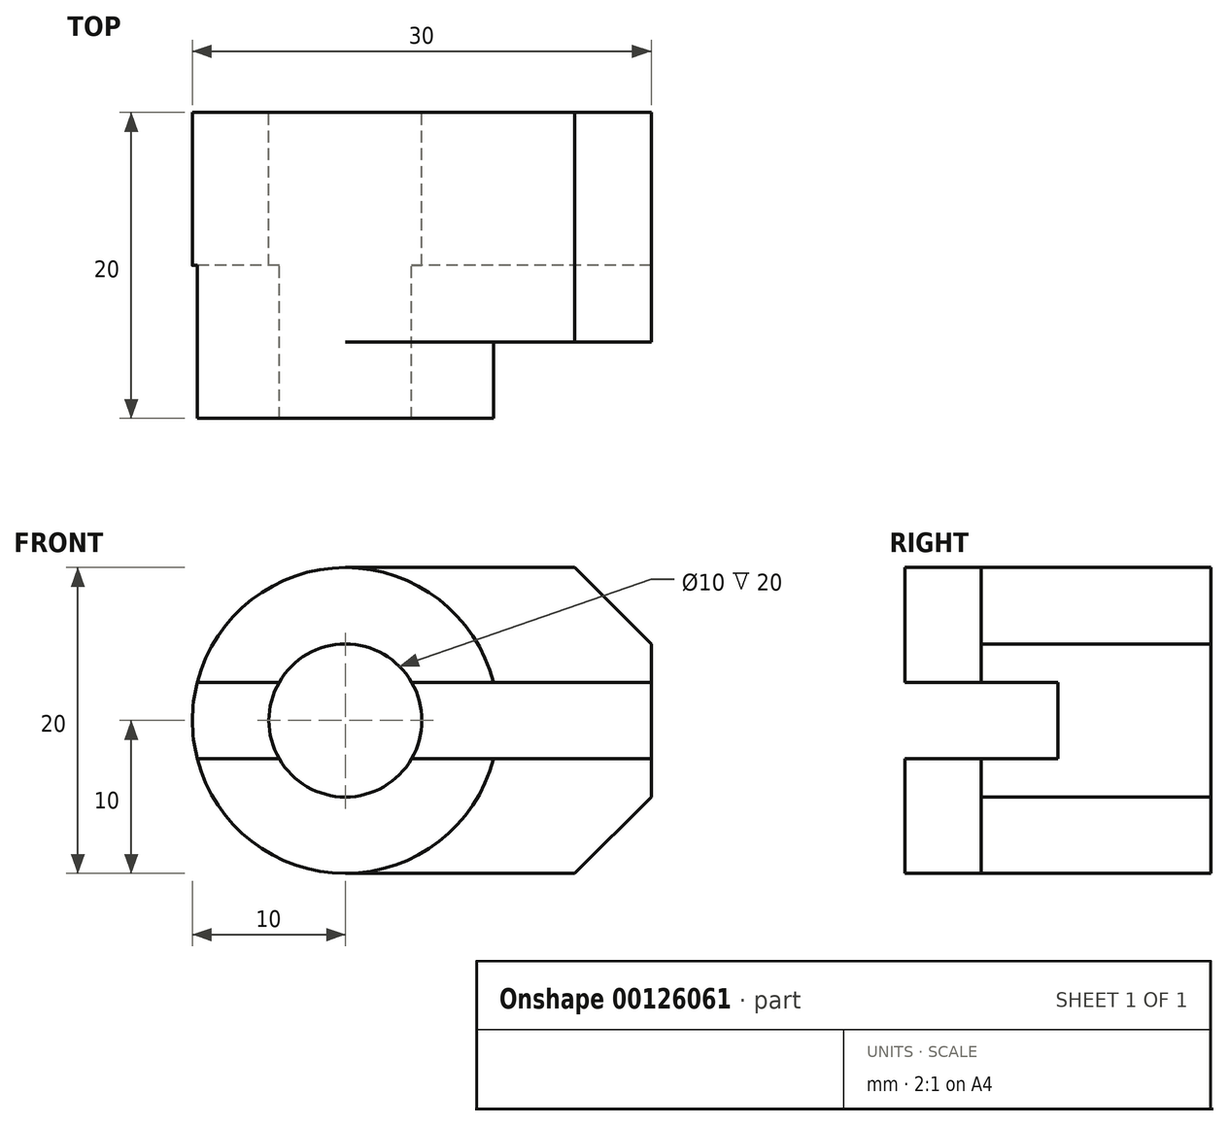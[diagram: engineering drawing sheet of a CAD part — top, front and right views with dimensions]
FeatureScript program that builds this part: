
annotation { "Feature Type Name" : "Feature", "Feature Type Description" : "" }
export const myFeature = defineFeature(function(context is Context, id is Id, definition is map)
    precondition{}
    {
        {
            var Q0;
            Q0=qCreatedBy(makeId("Front.planeOp"),FACE);
            var sketch = newSketch(context, id + "F0", { "sketchPlane" : qUnion([Q0])});
            skCircle(sketch, "E0", {"center": v(0, 0) * mm, "radius": 5 * mm});
            skCircle(sketch, "E1", {"center": v(0, 0) * mm, "radius": 10 * mm});
            skLineSegment(sketch, "E2", {"start": v(0, 10) * mm, "end": v(20, 10) * mm});
            skLineSegment(sketch, "E3", {"start": v(20, 10) * mm, "end": v(20, -10) * mm});
            skLineSegment(sketch, "E4", {"start": v(20, -10) * mm, "end": v(0, -10) * mm});
            skSolve(sketch);
        }
        {
            var Q0;
            Q0=makeQuery(id+"F0.imprint","IMPRINT",FACE,{"disambiguationData":[TD([[makeQuery(id+"F0.imprint","IMPRINT",EDGE,{"derivedFrom":sQuery(id+"F0.wireOp",EDGE,"E0")}),-1.0]])]});
            extrude(context, id + "F1", {"entities" : qUnion([Q0]), "depth" : 20 * mm});
        }
        {
            var Q0;
            {var subQ0=sQuery(id+"F0.wireOp",EDGE,"E2");Q0=makeQuery(id+"F0.imprint","IMPRINT",FACE,{"disambiguationData":[TD([[makeQuery(id+"F0.imprint","IMPRINT",EDGE,{"derivedFrom":subQ0}),-1.0]])]});}
            extrude(context, id + "F2", {"entities" : qUnion([Q0]), "operationType" : NewBodyOperationType.ADD, "depth" : 15 * mm});
        }
        {
            var Q0;
            Q0=makeQuery(id+"F2.opExtrude","SWEPT_EDGE",EDGE,{"disambiguationData":[OSD([sQuery(id+"F0.wireOp",EDGE,"E2"),sQuery(id+"F0.wireOp",EDGE,"E3")])]});
            var Q1;
            Q1=makeQuery(id+"F2.opExtrude","SWEPT_EDGE",EDGE,{"disambiguationData":[OSD([sQuery(id+"F0.wireOp",EDGE,"E3"),sQuery(id+"F0.wireOp",EDGE,"E4")])]});
            chamfer(context, id + "F3", {"entities" : qUnion([Q0, Q1]), "width" : 5 * mm, "tangentPropagation" : true});
        }
        {
            var Q0;
            Q0=qCreatedBy(makeId("Right.planeOp"),FACE);
            var sketch = newSketch(context, id + "F4", { "sketchPlane" : qUnion([Q0])});
            skLineSegment(sketch, "E5.bottom", {"start": v(-10, -2.5) * mm, "end": v(-20, -2.5) * mm});
            skLineSegment(sketch, "E5.top", {"start": v(-10, 2.5) * mm, "end": v(-20, 2.5) * mm});
            skLineSegment(sketch, "E5.left", {"start": v(-10, -2.5) * mm, "end": v(-10, 2.5) * mm});
            skLineSegment(sketch, "E5.right", {"start": v(-20, -2.5) * mm, "end": v(-20, 2.5) * mm});
            skSolve(sketch);
        }
        {
            var Q0;
            Q0 = qSketchRegion(id + "F4", true);
            extrude(context, id + "F5", {"entities" : qUnion([Q0]), "operationType" : NewBodyOperationType.REMOVE, "endBound" : BoundingType.SYMMETRIC, "depth" : 40 * mm});
        }
    });
